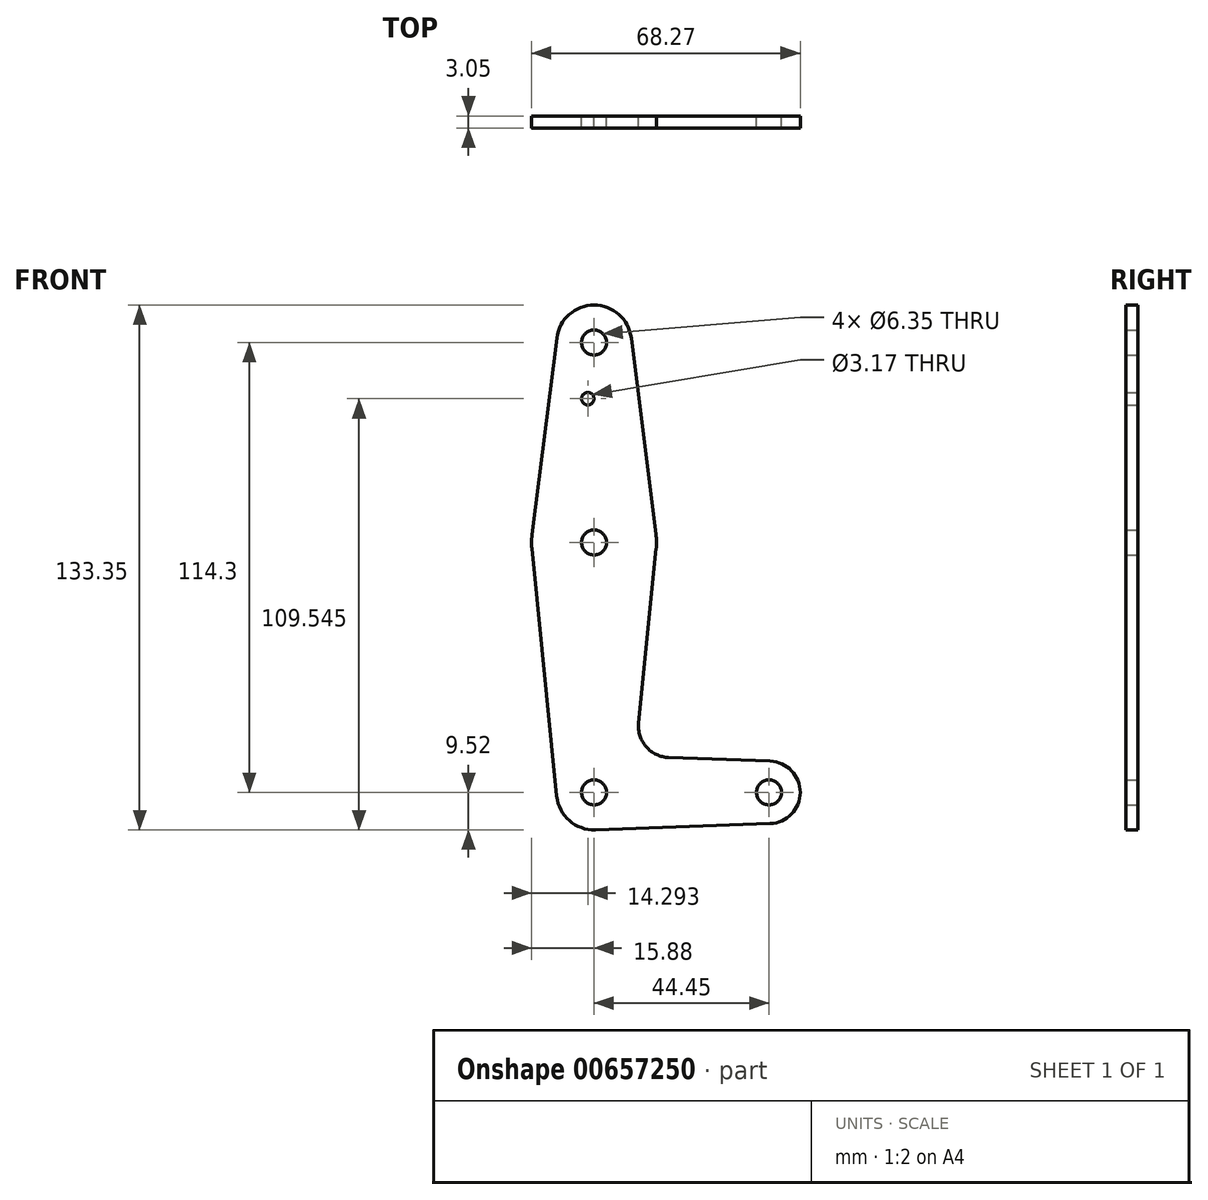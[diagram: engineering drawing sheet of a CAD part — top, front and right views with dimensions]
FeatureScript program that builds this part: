
annotation { "Feature Type Name" : "Feature", "Feature Type Description" : "" }
export const myFeature = defineFeature(function(context is Context, id is Id, definition is map)
    precondition{}
    {
        {
            var Q0;
            Q0=qCreatedBy(makeId("Front.planeOp"),FACE);
            var sketch = newSketch(context, id + "F0", { "sketchPlane" : qUnion([Q0])});
            skLineSegment(sketch, "E0", {"start": v(0, 0) * mm, "end": v(0, 114.3) * mm, "construction": true});
            skLineSegment(sketch, "E1", {"start": v(0, 0) * mm, "end": v(44.45, 0) * mm, "construction": true});
            skCircle(sketch, "E2", {"center": v(0, 114.3) * mm, "radius": 9.53 * mm});
            skCircle(sketch, "E3", {"center": v(0, 63.5) * mm, "radius": 15.88 * mm});
            skCircle(sketch, "E4", {"center": v(0, 0) * mm, "radius": 9.53 * mm});
            skCircle(sketch, "E5", {"center": v(44.45, 0) * mm, "radius": 7.94 * mm});
            skLineSegment(sketch, "E6", {"start": v(-15.75, 65.48) * mm, "end": v(-9.45, 115.5) * mm});
            skLineSegment(sketch, "E7", {"start": v(9.45, 115.5) * mm, "end": v(15.75, 65.48) * mm});
            skLineSegment(sketch, "E8", {"start": v(18.97, 8.85) * mm, "end": v(44.73, 7.93) * mm});
            skLineSegment(sketch, "E9", {"start": v(0.34, -9.52) * mm, "end": v(44.73, -7.93) * mm});
            skLineSegment(sketch, "E10", {"start": v(-15.8, 61.91) * mm, "end": v(-9.48, -0.95) * mm});
            skLineSegment(sketch, "E11", {"start": v(15.8, 61.91) * mm, "end": v(11.34, 17.6) * mm});
            skCircle(sketch, "E12", {"center": v(-1.59, 100.03) * mm, "radius": 1.59 * mm});
            skPoint(sketch, "E13.newPointA", {"position": v(9.48, -0.95) * mm});
            skArc(sketch, "E13.filletArc", {"start": v(11.34, 17.6) * mm, "mid": v(13.26, 11.57) * mm, "end": v(18.97, 8.85) * mm});
            skCircle(sketch, "E14", {"center": v(0, 114.3) * mm, "radius": 3.18 * mm});
            skCircle(sketch, "E15", {"center": v(0, 63.5) * mm, "radius": 3.18 * mm});
            skCircle(sketch, "E16", {"center": v(0, 0) * mm, "radius": 3.18 * mm});
            skCircle(sketch, "E17", {"center": v(44.45, 0) * mm, "radius": 3.18 * mm});
            skSolve(sketch);
        }
        {
            var Q0;
            Q0 = qSketchRegion(id + "F0", true);
            extrude(context, id + "F1", {"entities" : qUnion([Q0]), "depth" : 3.05 * mm, "offsetDistance" : 25.4 * mm});
        }
    });
